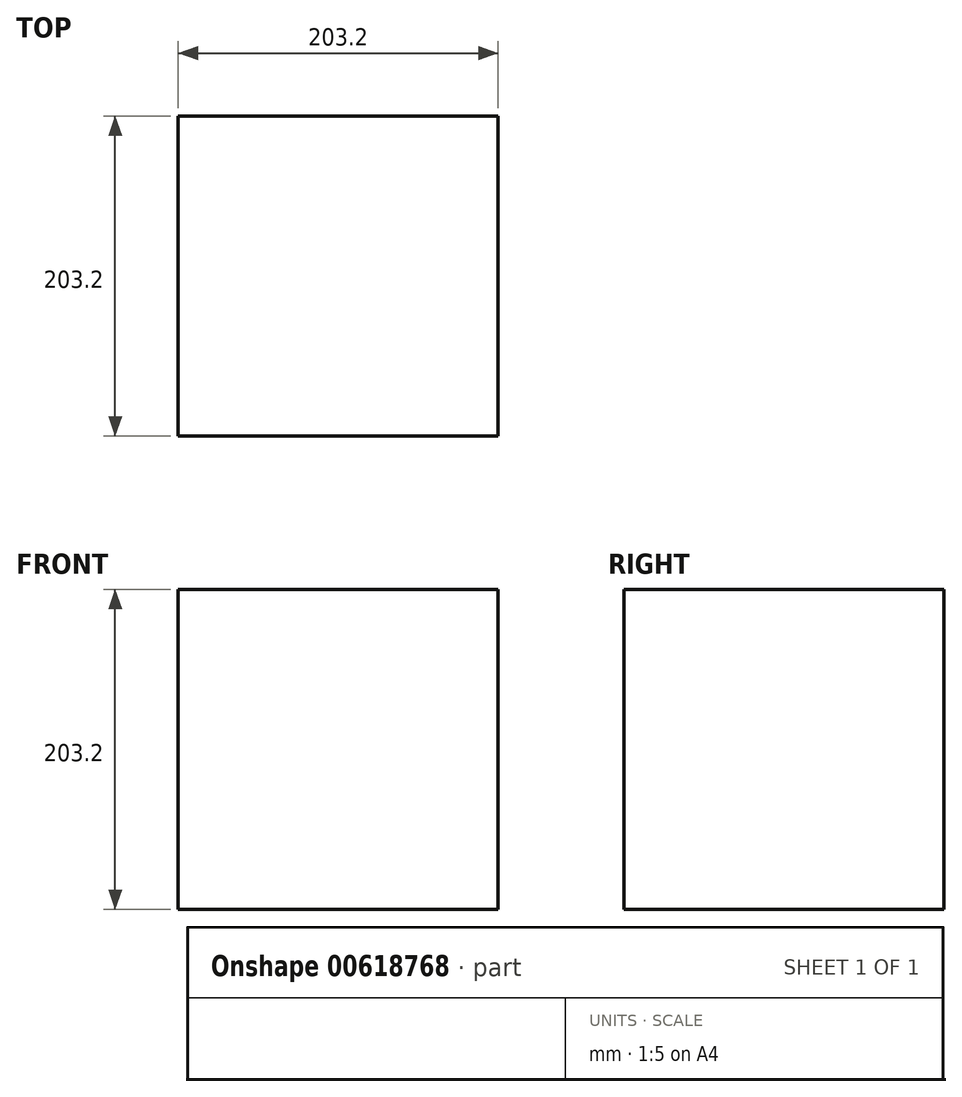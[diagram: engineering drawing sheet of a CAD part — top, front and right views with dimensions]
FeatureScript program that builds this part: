
annotation { "Feature Type Name" : "Feature", "Feature Type Description" : "" }
export const myFeature = defineFeature(function(context is Context, id is Id, definition is map)
    precondition{}
    {
        {
            var Q0;
            Q0=qCreatedBy(makeId("Top.planeOp"),FACE);
            var sketch = newSketch(context, id + "F0", { "sketchPlane" : qUnion([Q0])});
            skLineSegment(sketch, "E0.bottom", {"start": v(101.6, -101.6) * mm, "end": v(-101.6, -101.6) * mm});
            skLineSegment(sketch, "E0.top", {"start": v(101.6, 101.6) * mm, "end": v(-101.6, 101.6) * mm});
            skLineSegment(sketch, "E0.left", {"start": v(101.6, -101.6) * mm, "end": v(101.6, 101.6) * mm});
            skLineSegment(sketch, "E0.right", {"start": v(-101.6, -101.6) * mm, "end": v(-101.6, 101.6) * mm});
            skPoint(sketch, "E0.middle", {"position": v(0, 0) * mm});
            skSolve(sketch);
        }
        {
            var Q0;
            Q0 = qSketchRegion(id + "F0", true);
            extrude(context, id + "F1", {"entities" : qUnion([Q0]), "depth" : 203.2 * mm, "offsetDistance" : 25.4 * mm});
        }
    });
